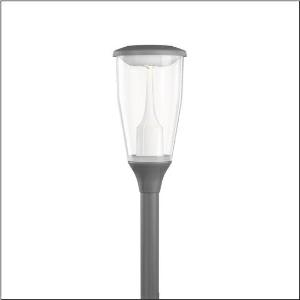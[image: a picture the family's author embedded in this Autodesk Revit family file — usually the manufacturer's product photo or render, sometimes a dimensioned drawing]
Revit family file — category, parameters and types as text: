
# Revit family: dl_11_iq___st1_2a_5xa5575kf14hp00022_6351
name_source: partatom
category: Lighting Fixtures
units: mm (PartAtom-declared; Revit-internal decimal feet)

## family parameters
Cut with Voids When Loaded = No
Host = Face
Light Source = No
Part Type = Normal
Room Calculation Point = No
Round Connector Dimension = Use Diameter
Shared = No

## types (1)
- --- (1 x LED, 5060 lm, 33.6 W, 4000K)
    Apparent Load = 34 VA
    CIE Flux Codes = 33 63 91 94 100
    Color Rendering = 70
    Color Temperature = 4000K
    Default Elevation = 1800 mm
    Description = DL 11 iQ, mast luminaire, Module 540 iQ-SR, primary light control with 3 zone facetted reflector, of plastic, silver coated, highly specular, structured, primary optical cover: cover, of PMMA, transparent, light distribution: ST1.2a, light emission: direct distribution, primary light characteristic: asymmetric, installation type: post-top, LED, High Power LED, light colour: 740, colour temperature: 4000K, control: Street-Remote, Auto-Match, Temp-Guard, Lumen-Switch, Night-Set, Smart-Wire, Light-Fading, Desk-Remote (wireless, voltage-free reading and setting of iQ features in the workshop via application-optimized NFC function/RFID function), optimised constant luminous flux control (CLO 2.0), mains connection: 220..240V, AC, 50/60Hz, connection cable pre-assembled, cable length: 5,5m, wiring characteristics: H07RN-F, 5-core, 1.5mm², start of lifetime: 34W, end of service life: 36W, luminaire housing, upper part, of diecast aluminium, coated, Siteco® metallic grey (DB 702S), spigot size: 76mm (post-top), post-top mast mounting element, of diecast aluminium, coated, Siteco® metallic grey (DB 702S), Module 540 iQ-SR, traffic white (RAL 9016), equipment: Power, protection rating (complete): IP66, insulation class (complete): insulation class II (safety insulation), certification: CE, ENEC, ENEC+, VDE, packaging unit: 1 piece

Light Distribution: ST1.2a
    Height = 665 mm
    Lamp = 1 x LED
    Lamp Light Flux = 5060 lm
    Lamp Power = 33.6 W
    Lamp count = 1
    Length = 334 mm
    Luminous efficacy = 151 lm/W
    Manufacturer = Siteco
    ModVariant = No
    Model = 5XA5575KF14HP00022
    Number of Poles = 1
    OnlyDefault = Yes
    Power Factor = 1
    Product Name = DL 11 iQ | ST1.2a
    Product group = mast luminaire | pylon top
    ProductGroupID = 6100
    Protection Class = Protection class II
    Protection Degree = IP 66
    RLX_Detail_Level = 1
    RLX_Emergency_Light_Flux = 0 lm
    RLX_Emergency_Type = 0
    RLX_Emergency_Type_DB = No
    RlxData = <blob elided: 102101 chars, md5=2023327c>
    Socket = socket
    Standby Power = 0 W
    System Light Flux = 5060 lm
    System Power = 34 W
    Type Comments = factory setting: luminous flux: 100 % | dim-lin: 254 | 695 mA
    Type Image = l_1258354.jpg
    URL = http://relux.com
    VarID = @adj_002499
    Voltage = 0 V
    Weight = 0.00 kg
    Width = 0 mm  [stored 0 ft]

note: [stored X ft] marks values corroborated as IEEE doubles in the binary element streams (Revit-internal decimal feet)

## geometry (parser evidence)
native form markers: Blend x4, Sweep x11
no freeform markers — native parametric forms only
